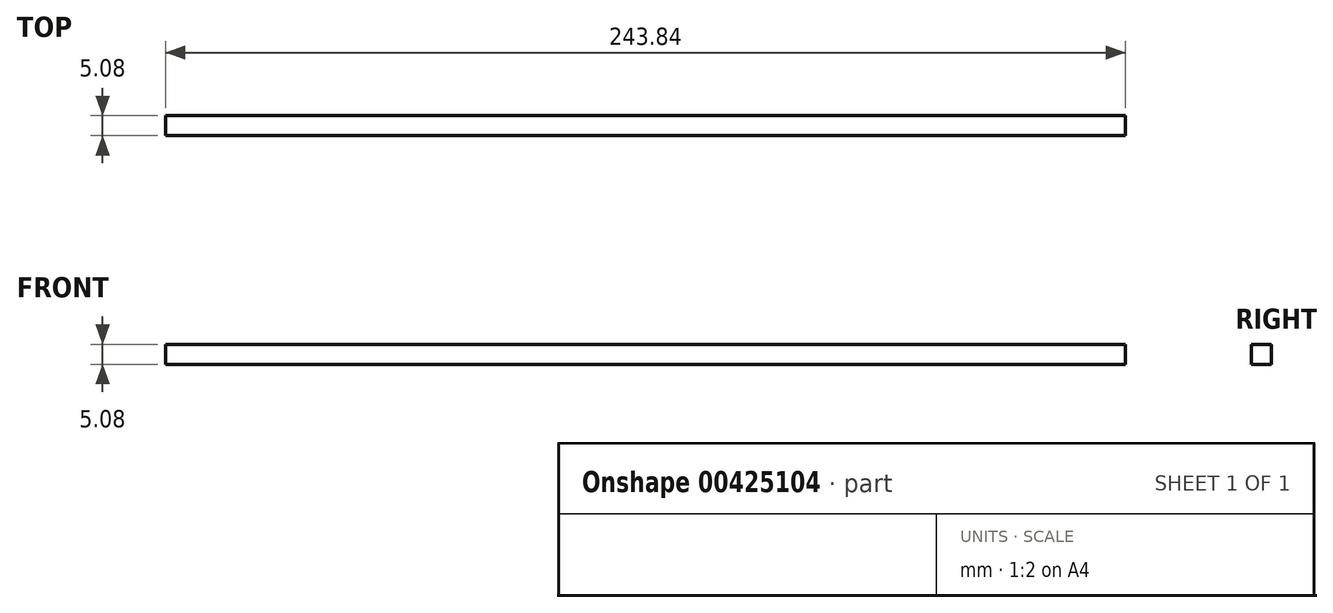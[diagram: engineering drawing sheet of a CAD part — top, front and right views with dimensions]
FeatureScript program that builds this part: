
annotation { "Feature Type Name" : "Feature", "Feature Type Description" : "" }
export const myFeature = defineFeature(function(context is Context, id is Id, definition is map)
    precondition{}
    {
        {
            var Q0;
            Q0=qCreatedBy(makeId("Front.planeOp"),FACE);
            var sketch = newSketch(context, id + "F0", { "sketchPlane" : qUnion([Q0])});
            skLineSegment(sketch, "E0.bottom", {"start": v(-128.27, -26.75) * mm, "end": v(115.57, -26.75) * mm});
            skLineSegment(sketch, "E0.top", {"start": v(-128.27, -31.83) * mm, "end": v(115.57, -31.83) * mm});
            skLineSegment(sketch, "E0.left", {"start": v(-128.27, -26.75) * mm, "end": v(-128.27, -31.83) * mm});
            skLineSegment(sketch, "E0.right", {"start": v(115.57, -26.75) * mm, "end": v(115.57, -31.83) * mm});
            skSolve(sketch);
        }
        {
            var Q0;
            Q0 = qSketchRegion(id + "F0", true);
            extrude(context, id + "F1", {"entities" : qUnion([Q0]), "depth" : 5.08 * mm});
        }
    });
